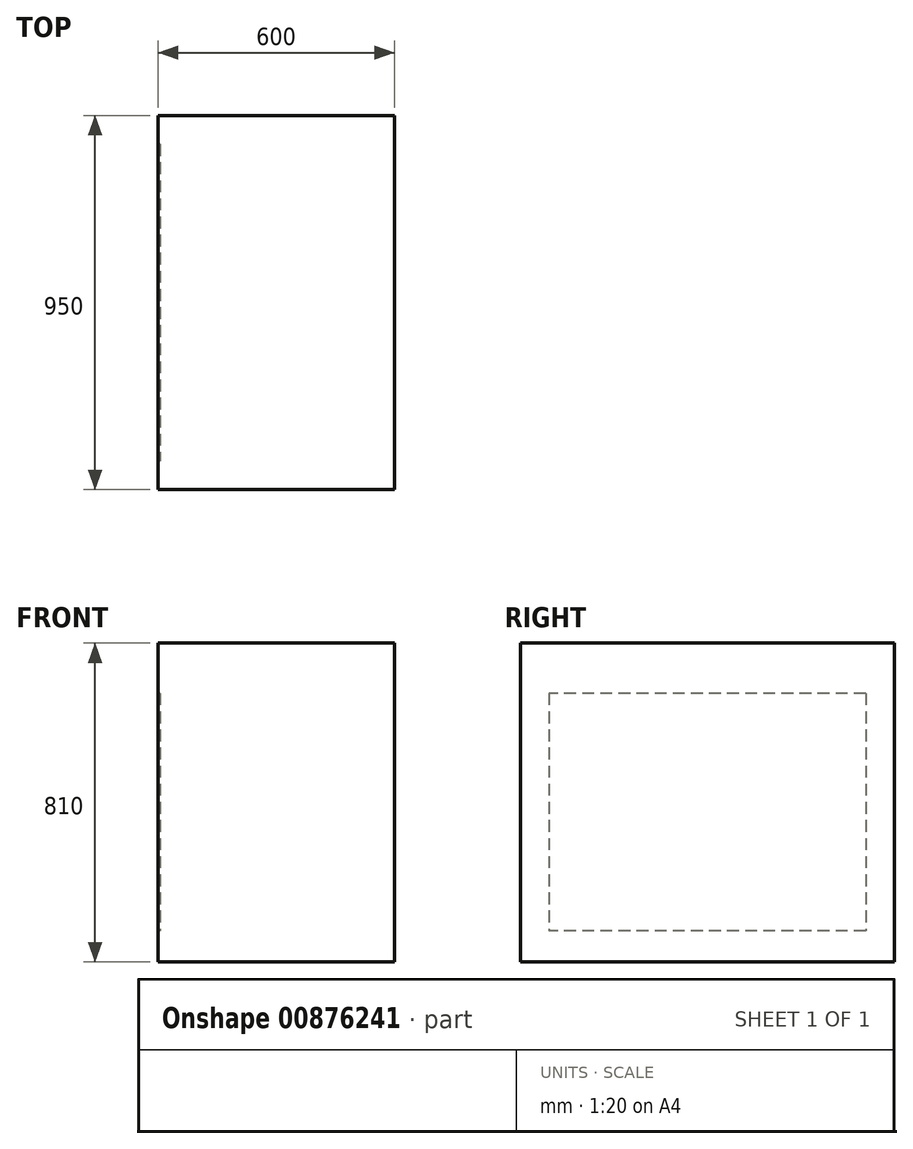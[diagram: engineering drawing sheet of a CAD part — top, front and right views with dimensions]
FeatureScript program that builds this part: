
annotation { "Feature Type Name" : "Feature", "Feature Type Description" : "" }
export const myFeature = defineFeature(function(context is Context, id is Id, definition is map)
    precondition{}
    {
        {
            var Q0;
            Q0=qCreatedBy(makeId("Front.planeOp"),FACE);
            var sketch = newSketch(context, id + "F0", { "sketchPlane" : qUnion([Q0])});
            skLineSegment(sketch, "E0.bottom", {"start": v(0, 0) * mm, "end": v(600, 0) * mm});
            skLineSegment(sketch, "E0.top", {"start": v(0, 810) * mm, "end": v(600, 810) * mm});
            skLineSegment(sketch, "E0.left", {"start": v(0, 0) * mm, "end": v(0, 810) * mm});
            skLineSegment(sketch, "E0.right", {"start": v(600, 0) * mm, "end": v(600, 810) * mm});
            skSolve(sketch);
        }
        {
            var Q0;
            Q0=makeQuery(id+"F0.imprint","IMPRINT",FACE,{"disambiguationData":[TD([[makeQuery(id+"F0.imprint","IMPRINT",EDGE,{"derivedFrom":sQuery(id+"F0.wireOp",EDGE,"E0.bottom")}),1.0]])]});
            extrude(context, id + "F1", {"entities" : qUnion([Q0]), "depth" : 950 * mm, "offsetDistance" : 25.4 * mm, "flatOperationType" : FlatOperationType.REMOVE, "domain" : OperationDomain.MODEL});
        }
        {
            var Q0;
            Q0=makeQuery(id+"F1.opExtrude","SWEPT_FACE",FACE,{"disambiguationData":[OSD([sQuery(id+"F0.wireOp",EDGE,"E0.left")])]});
            var sketch = newSketch(context, id + "F2", { "sketchPlane" : qUnion([Q0])});
            skLineSegment(sketch, "E1.bottom", {"start": v(72.44, 682.28) * mm, "end": v(876.99, 682.28) * mm});
            skLineSegment(sketch, "E1.top", {"start": v(72.44, 78.16) * mm, "end": v(876.99, 78.16) * mm});
            skLineSegment(sketch, "E1.left", {"start": v(72.44, 682.28) * mm, "end": v(72.44, 78.16) * mm});
            skLineSegment(sketch, "E1.right", {"start": v(876.99, 682.28) * mm, "end": v(876.99, 78.16) * mm});
            skSolve(sketch);
        }
        {
            var Q0;
            Q0=makeQuery(id+"F2.imprint","IMPRINT",FACE,{"disambiguationData":[TD([[makeQuery(id+"F2.imprint","IMPRINT",EDGE,{"derivedFrom":sQuery(id+"F2.wireOp",EDGE,"E1.bottom")}),-1.0]])]});
            extrude(context, id + "F3", {"entities" : qUnion([Q0]), "operationType" : NewBodyOperationType.REMOVE, "oppositeDirection" : true, "depth" : 5 * mm, "offsetDistance" : 25.4 * mm});
        }
    });
